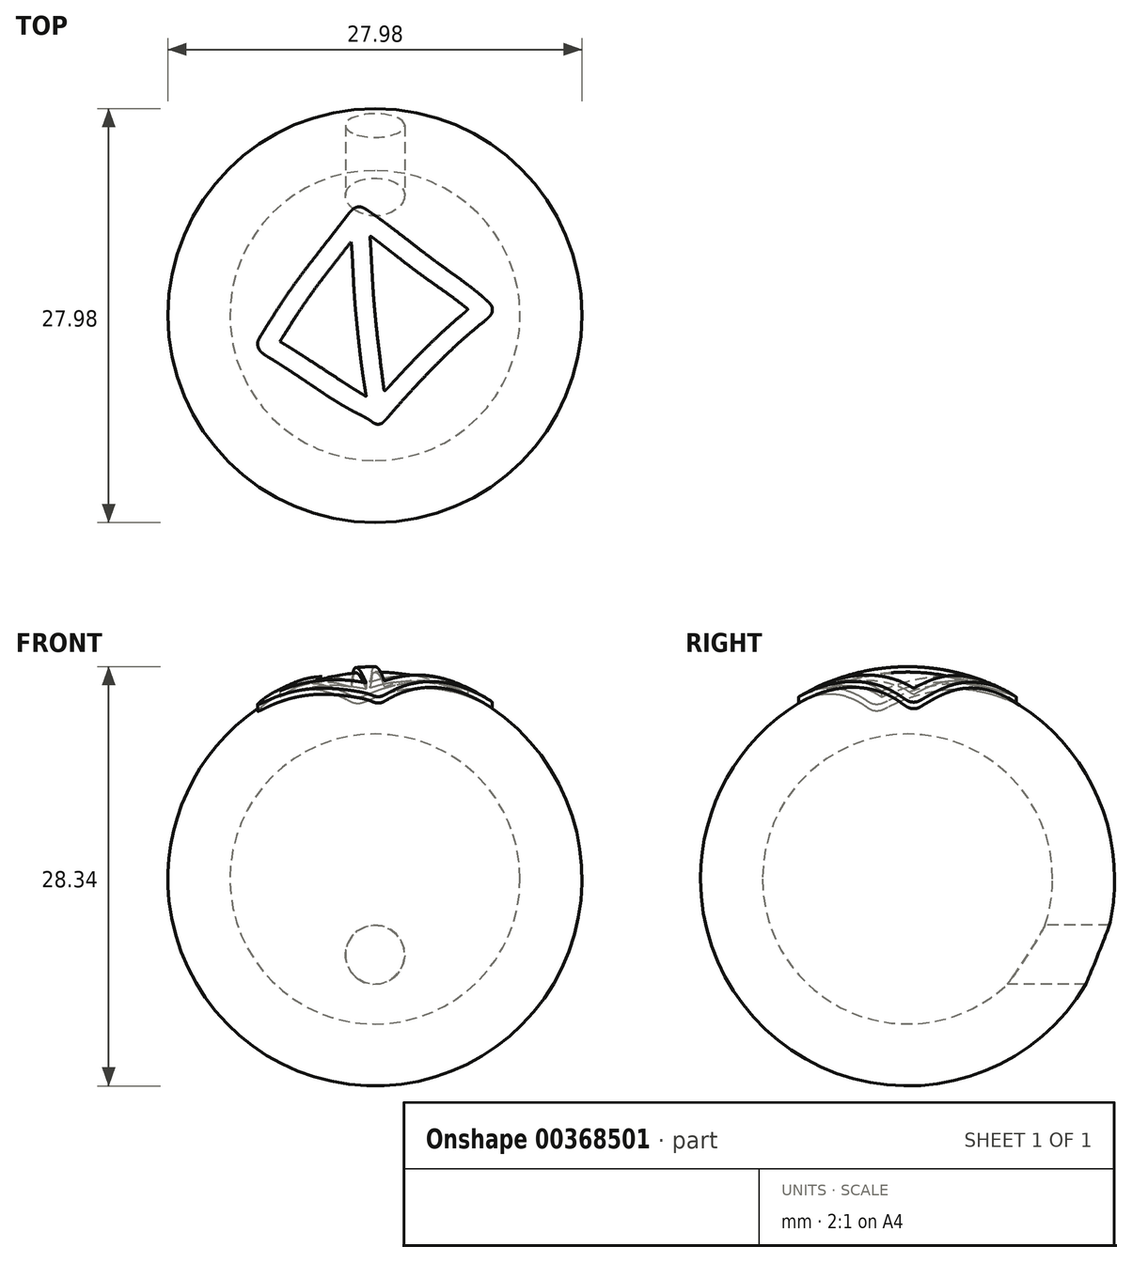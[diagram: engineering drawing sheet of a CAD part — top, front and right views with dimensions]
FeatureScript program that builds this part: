
annotation { "Feature Type Name" : "Feature", "Feature Type Description" : "" }
export const myFeature = defineFeature(function(context is Context, id is Id, definition is map)
    precondition{}
    {
        {
            var Q0;
            Q0=qCreatedBy(makeId("Top.planeOp"),FACE);
            var sketch = newSketch(context, id + "F0", { "sketchPlane" : qUnion([Q0])});
            skLineSegment(sketch, "E0", {"start": v(0, -10) * mm, "end": v(0, 10) * mm});
            skArc(sketch, "E1", {"start": v(0, 10) * mm, "mid": v(-10, 0) * mm, "end": v(0, -10) * mm});
            skSolve(sketch);
        }
        {
            var Q0;
            {var subQ0=sQuery(id+"F0.wireOp",EDGE,"E1");Q0=makeQuery(id+"F0.imprint","IMPRINT",FACE,{"disambiguationData":[TD([[makeQuery(id+"F0.imprint","IMPRINT",EDGE,{"derivedFrom":subQ0}),1.0]])]});}
            var Q1;
            Q1=sQuery(id+"F0.wireOp",EDGE,"E0");
            revolve(context, id + "F1", {"entities" : qUnion([Q0]), "axis" : qUnion([Q1]), "revolveType" : RevolveType.FULL});
        }
        {
            var Q0;
            Q0=makeQuery(id+"F1.opRevolve","SWEPT_BODY",BODY,{"disambiguationData":[OSD([sQuery(id+"F0.wireOp",EDGE,"E0"),sQuery(id+"F0.wireOp",EDGE,"E1")])]});
            var Q1;
            Q1=sQuery(id+"F0.wireOp",VERTEX,"NPe4G0ez-t7S9-9isL-QO5v-uuJu600mHcIT.center");
            var Q2;
            Q2=sQuery(id+"F0.wireOp",VERTEX,"E1.center");
            transform(context, id + "F2", {"entities" : qUnion([Q0]), "transformType" : TransformType.SCALE_UNIFORMLY, "scale" : 33.3, "scalePoint" : qUnion([Q2]), "makeCopy" : false});
        }
        {
            var Q0;
            Q0=qCreatedBy(makeId("Top.planeOp"),FACE);
            var sketch = newSketch(context, id + "F3", { "sketchPlane" : qUnion([Q0])});
            skArc(sketch, "E2", {"start": v(-33, 172.81) * mm, "mid": v(-34.37, 171.98) * mm, "end": v(-35.66, 171) * mm});
            skArc(sketch, "E3", {"start": v(-35.66, 171) * mm, "mid": v(-37.15, 169.67) * mm, "end": v(-38.56, 168.26) * mm});
            skArc(sketch, "E4", {"start": v(-38.56, 168.26) * mm, "mid": v(-40.37, 166.25) * mm, "end": v(-42.1, 164.18) * mm});
            skArc(sketch, "E5", {"start": v(-42.1, 164.18) * mm, "mid": v(-44.55, 161.1) * mm, "end": v(-46.95, 157.98) * mm});
            skArc(sketch, "E6", {"start": v(-46.95, 157.98) * mm, "mid": v(-49.6, 154.52) * mm, "end": v(-52.25, 151.08) * mm});
            skArc(sketch, "E7", {"start": v(-52.25, 151.08) * mm, "mid": v(-56.88, 145.1) * mm, "end": v(-61.52, 139.12) * mm});
            skArc(sketch, "E8", {"start": v(-61.52, 139.12) * mm, "mid": v(-66.9, 132.2) * mm, "end": v(-72.28, 125.28) * mm});
            skArc(sketch, "E9", {"start": v(-72.28, 125.28) * mm, "mid": v(-77.76, 118.26) * mm, "end": v(-83.25, 111.24) * mm});
            skArc(sketch, "E10", {"start": v(-83.25, 111.24) * mm, "mid": v(-97.95, 92.31) * mm, "end": v(-112.54, 73.3) * mm});
            skArc(sketch, "E11", {"start": v(-112.54, 73.3) * mm, "mid": v(-122.82, 59.57) * mm, "end": v(-132.87, 45.67) * mm});
            skArc(sketch, "E12", {"start": v(-132.87, 45.67) * mm, "mid": v(-142, 32.54) * mm, "end": v(-150.9, 19.25) * mm});
            skArc(sketch, "E13", {"start": v(-150.9, 19.25) * mm, "mid": v(-161.66, 2.63) * mm, "end": v(-172.26, -14.1) * mm});
            skArc(sketch, "E14", {"start": v(-172.26, -14.1) * mm, "mid": v(-177.97, -23.22) * mm, "end": v(-183.64, -32.36) * mm});
            skArc(sketch, "E15", {"start": v(-183.64, -32.36) * mm, "mid": v(-185.48, -35.48) * mm, "end": v(-187.18, -38.67) * mm});
            skArc(sketch, "E16", {"start": v(-187.18, -38.67) * mm, "mid": v(-188, -40.65) * mm, "end": v(-188.56, -42.72) * mm});
            skArc(sketch, "E17", {"start": v(-188.56, -42.72) * mm, "mid": v(-188.82, -44.8) * mm, "end": v(-188.77, -46.88) * mm});
            skArc(sketch, "E18", {"start": v(-188.77, -46.88) * mm, "mid": v(-188.23, -49.88) * mm, "end": v(-187.2, -52.73) * mm});
            skArc(sketch, "E19", {"start": v(-187.2, -52.73) * mm, "mid": v(-185.68, -55.44) * mm, "end": v(-183.75, -57.87) * mm});
            skArc(sketch, "E20", {"start": v(-183.75, -57.87) * mm, "mid": v(-180.92, -60.6) * mm, "end": v(-177.8, -63) * mm});
            skArc(sketch, "E21", {"start": v(-177.8, -63) * mm, "mid": v(-173.08, -66.1) * mm, "end": v(-168.25, -69) * mm});
            skArc(sketch, "E22", {"start": v(-168.25, -69) * mm, "mid": v(-164.73, -71.07) * mm, "end": v(-161.26, -73.21) * mm});
            skArc(sketch, "E23", {"start": v(-161.26, -73.21) * mm, "mid": v(-155.32, -76.99) * mm, "end": v(-149.4, -80.79) * mm});
            skArc(sketch, "E24", {"start": v(-149.4, -80.79) * mm, "mid": v(-142.56, -85.22) * mm, "end": v(-135.75, -89.69) * mm});
            skArc(sketch, "E25", {"start": v(-135.75, -89.69) * mm, "mid": v(-128.86, -94.25) * mm, "end": v(-122, -98.84) * mm});
            skArc(sketch, "E26", {"start": v(-122, -98.84) * mm, "mid": v(-115.2, -103.41) * mm, "end": v(-108.4, -107.98) * mm});
            skArc(sketch, "E27", {"start": v(-108.4, -107.98) * mm, "mid": v(-101.82, -112.4) * mm, "end": v(-95.25, -116.8) * mm});
            skArc(sketch, "E28", {"start": v(-95.25, -116.8) * mm, "mid": v(-89.63, -120.57) * mm, "end": v(-84.02, -124.33) * mm});
            skArc(sketch, "E29", {"start": v(-84.02, -124.33) * mm, "mid": v(-81, -126.34) * mm, "end": v(-78, -128.35) * mm});
            skArc(sketch, "E30", {"start": v(-78, -128.35) * mm, "mid": v(-71.4, -132.67) * mm, "end": v(-64.72, -136.88) * mm});
            skArc(sketch, "E31", {"start": v(-64.72, -136.88) * mm, "mid": v(-57.8, -141.12) * mm, "end": v(-50.8, -145.26) * mm});
            skArc(sketch, "E32", {"start": v(-50.8, -145.26) * mm, "mid": v(-44.03, -149.14) * mm, "end": v(-37.21, -152.92) * mm});
            skArc(sketch, "E33", {"start": v(-37.21, -152.92) * mm, "mid": v(-31.14, -156.15) * mm, "end": v(-25, -159.25) * mm});
            skArc(sketch, "E34", {"start": v(-25, -159.25) * mm, "mid": v(-22.06, -160.7) * mm, "end": v(-19.16, -162.22) * mm});
            skArc(sketch, "E35", {"start": v(-19.16, -162.22) * mm, "mid": v(-16.38, -163.71) * mm, "end": v(-13.63, -165.25) * mm});
            skArc(sketch, "E36", {"start": v(-13.63, -165.25) * mm, "mid": v(-11.31, -166.6) * mm, "end": v(-9.01, -168) * mm});
            skArc(sketch, "E37", {"start": v(-9.01, -168) * mm, "mid": v(-7.81, -168.8) * mm, "end": v(-6.69, -169.7) * mm});
            skArc(sketch, "E38", {"start": v(-6.69, -169.7) * mm, "mid": v(-4.48, -171.46) * mm, "end": v(-2.12, -173) * mm});
            skArc(sketch, "E39", {"start": v(-2.12, -173) * mm, "mid": v(0.04, -174.03) * mm, "end": v(2.34, -174.72) * mm});
            skArc(sketch, "E40", {"start": v(2.34, -174.72) * mm, "mid": v(4.5, -174.99) * mm, "end": v(6.69, -174.86) * mm});
            skArc(sketch, "E41", {"start": v(6.69, -174.86) * mm, "mid": v(8.87, -174.35) * mm, "end": v(10.94, -173.5) * mm});
            skArc(sketch, "E42", {"start": v(10.94, -173.5) * mm, "mid": v(11.75, -173) * mm, "end": v(12.5, -172.4) * mm});
            skArc(sketch, "E43", {"start": v(12.5, -172.4) * mm, "mid": v(13.95, -171) * mm, "end": v(15.38, -169.59) * mm});
            skArc(sketch, "E44", {"start": v(15.38, -169.59) * mm, "mid": v(17.06, -167.86) * mm, "end": v(18.7, -166.1) * mm});
            skArc(sketch, "E45", {"start": v(18.7, -166.1) * mm, "mid": v(20.42, -164.19) * mm, "end": v(22.1, -162.24) * mm});
            skArc(sketch, "E46", {"start": v(22.1, -162.24) * mm, "mid": v(32.46, -150.21) * mm, "end": v(42.96, -138.3) * mm});
            skArc(sketch, "E47", {"start": v(42.96, -138.3) * mm, "mid": v(54.31, -125.7) * mm, "end": v(65.78, -113.23) * mm});
            skArc(sketch, "E48", {"start": v(65.78, -113.23) * mm, "mid": v(77.16, -101.09) * mm, "end": v(88.65, -89.06) * mm});
            skArc(sketch, "E49", {"start": v(88.65, -89.06) * mm, "mid": v(99.07, -78.41) * mm, "end": v(109.64, -67.9) * mm});
            skArc(sketch, "E50", {"start": v(109.64, -67.9) * mm, "mid": v(117.81, -59.96) * mm, "end": v(126.06, -52.09) * mm});
            skArc(sketch, "E51", {"start": v(126.06, -52.09) * mm, "mid": v(133.02, -45.6) * mm, "end": v(140.08, -39.23) * mm});
            skArc(sketch, "E52", {"start": v(140.08, -39.23) * mm, "mid": v(147.61, -32.64) * mm, "end": v(155.23, -26.15) * mm});
            skArc(sketch, "E53", {"start": v(155.23, -26.15) * mm, "mid": v(165.3, -17.77) * mm, "end": v(175.42, -9.46) * mm});
            skArc(sketch, "E54", {"start": v(175.42, -9.46) * mm, "mid": v(179.05, -6.39) * mm, "end": v(182.58, -3.2) * mm});
            skArc(sketch, "E55", {"start": v(182.58, -3.2) * mm, "mid": v(184.71, -0.94) * mm, "end": v(186.58, 1.54) * mm});
            skArc(sketch, "E56", {"start": v(186.58, 1.54) * mm, "mid": v(187.71, 3.63) * mm, "end": v(188.46, 5.89) * mm});
            skArc(sketch, "E57", {"start": v(188.46, 5.89) * mm, "mid": v(188.81, 8.25) * mm, "end": v(188.75, 10.64) * mm});
            skArc(sketch, "E58", {"start": v(188.75, 10.64) * mm, "mid": v(188.42, 12.49) * mm, "end": v(187.86, 14.28) * mm});
            skArc(sketch, "E59", {"start": v(187.86, 14.28) * mm, "mid": v(187.09, 15.92) * mm, "end": v(186.1, 17.44) * mm});
            skArc(sketch, "E60", {"start": v(186.1, 17.44) * mm, "mid": v(184.48, 19.41) * mm, "end": v(182.72, 21.24) * mm});
            skArc(sketch, "E61", {"start": v(182.72, 21.24) * mm, "mid": v(179.3, 24.49) * mm, "end": v(175.84, 27.68) * mm});
            skArc(sketch, "E62", {"start": v(175.84, 27.68) * mm, "mid": v(171.1, 31.88) * mm, "end": v(166.27, 35.95) * mm});
            skArc(sketch, "E63", {"start": v(166.27, 35.95) * mm, "mid": v(160.23, 40.83) * mm, "end": v(154.12, 45.63) * mm});
            skArc(sketch, "E64", {"start": v(154.12, 45.63) * mm, "mid": v(146.93, 51.13) * mm, "end": v(139.67, 56.53) * mm});
            skArc(sketch, "E65", {"start": v(139.67, 56.53) * mm, "mid": v(131.36, 62.6) * mm, "end": v(123, 68.58) * mm});
            skArc(sketch, "E66", {"start": v(123, 68.58) * mm, "mid": v(114.4, 74.72) * mm, "end": v(105.83, 80.91) * mm});
            skArc(sketch, "E67", {"start": v(105.83, 80.91) * mm, "mid": v(98.5, 86.27) * mm, "end": v(91.21, 91.69) * mm});
            skArc(sketch, "E68", {"start": v(91.21, 91.69) * mm, "mid": v(83.18, 97.75) * mm, "end": v(75.19, 103.87) * mm});
            skArc(sketch, "E69", {"start": v(75.19, 103.87) * mm, "mid": v(64.09, 112.45) * mm, "end": v(53, 121.05) * mm});
            skArc(sketch, "E70", {"start": v(53, 121.05) * mm, "mid": v(42.99, 128.83) * mm, "end": v(32.94, 136.58) * mm});
            skArc(sketch, "E71", {"start": v(32.94, 136.58) * mm, "mid": v(25.36, 142.38) * mm, "end": v(17.73, 148.12) * mm});
            skArc(sketch, "E72", {"start": v(17.73, 148.12) * mm, "mid": v(11.29, 152.88) * mm, "end": v(4.8, 157.6) * mm});
            skArc(sketch, "E73", {"start": v(4.8, 157.6) * mm, "mid": v(-1.5, 162.08) * mm, "end": v(-7.86, 166.51) * mm});
            skArc(sketch, "E74", {"start": v(-7.86, 166.51) * mm, "mid": v(-12.3, 169.46) * mm, "end": v(-16.82, 172.26) * mm});
            skArc(sketch, "E75", {"start": v(-16.82, 172.26) * mm, "mid": v(-19.64, 173.67) * mm, "end": v(-22.64, 174.66) * mm});
            skArc(sketch, "E76", {"start": v(-22.64, 174.66) * mm, "mid": v(-25.1, 175) * mm, "end": v(-27.56, 174.77) * mm});
            skArc(sketch, "E77", {"start": v(-27.56, 174.77) * mm, "mid": v(-30.35, 173.98) * mm, "end": v(-33, 172.81) * mm});
            skArc(sketch, "E78", {"start": v(2.5, 120.65) * mm, "mid": v(4.7, 119) * mm, "end": v(6.88, 117.32) * mm});
            skArc(sketch, "E79", {"start": v(6.88, 117.32) * mm, "mid": v(10.53, 114.5) * mm, "end": v(14.18, 111.67) * mm});
            skArc(sketch, "E80", {"start": v(14.18, 111.67) * mm, "mid": v(18.38, 108.4) * mm, "end": v(22.57, 105.14) * mm});
            skArc(sketch, "E81", {"start": v(22.57, 105.14) * mm, "mid": v(26.8, 101.84) * mm, "end": v(31, 98.53) * mm});
            skArc(sketch, "E82", {"start": v(31, 98.53) * mm, "mid": v(40.47, 91.14) * mm, "end": v(49.96, 83.78) * mm});
            skArc(sketch, "E83", {"start": v(49.96, 83.78) * mm, "mid": v(57.43, 78.07) * mm, "end": v(64.95, 72.41) * mm});
            skArc(sketch, "E84", {"start": v(64.95, 72.41) * mm, "mid": v(72.33, 66.96) * mm, "end": v(79.75, 61.57) * mm});
            skArc(sketch, "E85", {"start": v(79.75, 61.57) * mm, "mid": v(88.87, 55.05) * mm, "end": v(98, 48.58) * mm});
            skArc(sketch, "E86", {"start": v(98, 48.58) * mm, "mid": v(108.94, 40.81) * mm, "end": v(119.82, 32.97) * mm});
            skArc(sketch, "E87", {"start": v(119.82, 32.97) * mm, "mid": v(127.9, 27) * mm, "end": v(135.87, 20.91) * mm});
            skArc(sketch, "E88", {"start": v(135.87, 20.91) * mm, "mid": v(142.08, 16.05) * mm, "end": v(148.26, 11.14) * mm});
            skArc(sketch, "E89", {"start": v(148.26, 11.14) * mm, "mid": v(148.87, 10.2) * mm, "end": v(148.8, 9.07) * mm});
            skArc(sketch, "E90", {"start": v(148.8, 9.07) * mm, "mid": v(148.66, 8.82) * mm, "end": v(148.47, 8.6) * mm});
            skArc(sketch, "E91", {"start": v(148.47, 8.6) * mm, "mid": v(147.14, 7.42) * mm, "end": v(145.8, 6.25) * mm});
            skArc(sketch, "E92", {"start": v(145.8, 6.25) * mm, "mid": v(144.24, 4.89) * mm, "end": v(142.67, 3.54) * mm});
            skArc(sketch, "E93", {"start": v(142.67, 3.54) * mm, "mid": v(140.84, 2) * mm, "end": v(139, 0.47) * mm});
            skArc(sketch, "E94", {"start": v(139, 0.47) * mm, "mid": v(126.28, -10.36) * mm, "end": v(113.83, -21.52) * mm});
            skArc(sketch, "E95", {"start": v(113.83, -21.52) * mm, "mid": v(99.63, -34.82) * mm, "end": v(85.65, -48.36) * mm});
            skArc(sketch, "E96", {"start": v(85.65, -48.36) * mm, "mid": v(70.67, -63.33) * mm, "end": v(55.94, -78.53) * mm});
            skArc(sketch, "E97", {"start": v(55.94, -78.53) * mm, "mid": v(40.89, -94.52) * mm, "end": v(26.07, -110.7) * mm});
            skArc(sketch, "E98", {"start": v(26.07, -110.7) * mm, "mid": v(24.28, -112.68) * mm, "end": v(22.47, -114.64) * mm});
            skArc(sketch, "E99", {"start": v(22.47, -114.64) * mm, "mid": v(20.9, -116.3) * mm, "end": v(19.32, -117.95) * mm});
            skArc(sketch, "E100", {"start": v(19.32, -117.95) * mm, "mid": v(17.95, -119.36) * mm, "end": v(16.56, -120.76) * mm});
            skArc(sketch, "E101", {"start": v(16.56, -120.76) * mm, "mid": v(16.35, -120.9) * mm, "end": v(16.1, -120.96) * mm});
            skArc(sketch, "E102", {"start": v(16.1, -120.96) * mm, "mid": v(14.93, -120.52) * mm, "end": v(14.34, -119.42) * mm});
            skArc(sketch, "E103", {"start": v(14.34, -119.42) * mm, "mid": v(11.4, -96.18) * mm, "end": v(8.47, -72.95) * mm});
            skArc(sketch, "E104", {"start": v(8.47, -72.95) * mm, "mid": v(5.63, -49.46) * mm, "end": v(2.99, -25.95) * mm});
            skArc(sketch, "E105", {"start": v(2.99, -25.95) * mm, "mid": v(0.67, -3.46) * mm, "end": v(-1.44, 19.04) * mm});
            skArc(sketch, "E106", {"start": v(-1.44, 19.04) * mm, "mid": v(-1.82, 23.65) * mm, "end": v(-2.17, 28.26) * mm});
            skArc(sketch, "E107", {"start": v(-2.17, 28.26) * mm, "mid": v(-2.65, 35.41) * mm, "end": v(-3.12, 42.56) * mm});
            skArc(sketch, "E108", {"start": v(-3.12, 42.56) * mm, "mid": v(-3.62, 50.64) * mm, "end": v(-4.1, 58.71) * mm});
            skArc(sketch, "E109", {"start": v(-4.1, 58.71) * mm, "mid": v(-4.55, 66.63) * mm, "end": v(-4.98, 74.54) * mm});
            skArc(sketch, "E110", {"start": v(-4.98, 74.54) * mm, "mid": v(-5.38, 82.1) * mm, "end": v(-5.8, 89.67) * mm});
            skArc(sketch, "E111", {"start": v(-5.8, 89.67) * mm, "mid": v(-6.18, 96.69) * mm, "end": v(-6.58, 103.7) * mm});
            skArc(sketch, "E112", {"start": v(-6.58, 103.7) * mm, "mid": v(-6.92, 109.59) * mm, "end": v(-7.27, 115.47) * mm});
            skArc(sketch, "E113", {"start": v(-7.27, 115.47) * mm, "mid": v(-7.43, 117.96) * mm, "end": v(-7.62, 120.44) * mm});
            skArc(sketch, "E114", {"start": v(-7.62, 120.44) * mm, "mid": v(-7.85, 123.46) * mm, "end": v(-8.01, 126.48) * mm});
            skArc(sketch, "E115", {"start": v(-8.01, 126.48) * mm, "mid": v(-7.8, 127.05) * mm, "end": v(-7.26, 127.3) * mm});
            skArc(sketch, "E116", {"start": v(-7.26, 127.3) * mm, "mid": v(-6.45, 127.17) * mm, "end": v(-5.73, 126.8) * mm});
            skArc(sketch, "E117", {"start": v(-5.73, 126.8) * mm, "mid": v(-1.6, 123.74) * mm, "end": v(2.5, 120.65) * mm});
            skArc(sketch, "E118", {"start": v(-35.55, 75.04) * mm, "mid": v(-34.77, 59.8) * mm, "end": v(-33.94, 44.56) * mm});
            skArc(sketch, "E119", {"start": v(-33.94, 44.56) * mm, "mid": v(-33.32, 34.26) * mm, "end": v(-32.6, 23.96) * mm});
            skArc(sketch, "E120", {"start": v(-32.6, 23.96) * mm, "mid": v(-31.84, 14.28) * mm, "end": v(-30.97, 4.61) * mm});
            skArc(sketch, "E121", {"start": v(-30.97, 4.61) * mm, "mid": v(-29.73, -8.18) * mm, "end": v(-28.43, -20.96) * mm});
            skArc(sketch, "E122", {"start": v(-28.43, -20.96) * mm, "mid": v(-26.87, -35.75) * mm, "end": v(-25.25, -50.53) * mm});
            skArc(sketch, "E123", {"start": v(-25.25, -50.53) * mm, "mid": v(-23.89, -62.47) * mm, "end": v(-22.44, -74.39) * mm});
            skArc(sketch, "E124", {"start": v(-22.44, -74.39) * mm, "mid": v(-21.14, -84.39) * mm, "end": v(-19.77, -94.38) * mm});
            skArc(sketch, "E125", {"start": v(-19.77, -94.38) * mm, "mid": v(-18.47, -103.17) * mm, "end": v(-17.06, -111.95) * mm});
            skArc(sketch, "E126", {"start": v(-17.06, -111.95) * mm, "mid": v(-16.5, -115.31) * mm, "end": v(-15.96, -118.68) * mm});
            skArc(sketch, "E127", {"start": v(-15.96, -118.68) * mm, "mid": v(-15.5, -121.53) * mm, "end": v(-15.07, -124.38) * mm});
            skArc(sketch, "E128", {"start": v(-15.07, -124.38) * mm, "mid": v(-14.7, -126.92) * mm, "end": v(-14.32, -129.45) * mm});
            skArc(sketch, "E129", {"start": v(-14.32, -129.45) * mm, "mid": v(-14.33, -129.58) * mm, "end": v(-14.4, -129.7) * mm});
            skArc(sketch, "E130", {"start": v(-14.4, -129.7) * mm, "mid": v(-14.77, -129.88) * mm, "end": v(-15.17, -129.79) * mm});
            skArc(sketch, "E131", {"start": v(-15.17, -129.79) * mm, "mid": v(-21.77, -125.75) * mm, "end": v(-28.36, -121.71) * mm});
            skArc(sketch, "E132", {"start": v(-28.36, -121.71) * mm, "mid": v(-35.1, -117.53) * mm, "end": v(-41.81, -113.3) * mm});
            skArc(sketch, "E133", {"start": v(-41.81, -113.3) * mm, "mid": v(-48.42, -109.06) * mm, "end": v(-55, -104.77) * mm});
            skArc(sketch, "E134", {"start": v(-55, -104.77) * mm, "mid": v(-69.13, -95.47) * mm, "end": v(-83.29, -86.18) * mm});
            skArc(sketch, "E135", {"start": v(-83.29, -86.18) * mm, "mid": v(-95.7, -78.09) * mm, "end": v(-108.12, -70.02) * mm});
            skArc(sketch, "E136", {"start": v(-108.12, -70.02) * mm, "mid": v(-118.2, -63.5) * mm, "end": v(-128.3, -57.02) * mm});
            skArc(sketch, "E137", {"start": v(-128.3, -57.02) * mm, "mid": v(-134.23, -53.26) * mm, "end": v(-140.2, -49.57) * mm});
            skLineSegment(sketch, "E138", {"start": v(-140.2, -49.57) * mm, "end": v(-152.92, -41.82) * mm});
            skLineSegment(sketch, "E139", {"start": v(-152.92, -41.82) * mm, "end": v(-147.8, -33.64) * mm});
            skArc(sketch, "E140", {"start": v(-147.8, -33.64) * mm, "mid": v(-136.62, -15.94) * mm, "end": v(-125.26, 1.64) * mm});
            skArc(sketch, "E141", {"start": v(-125.26, 1.64) * mm, "mid": v(-115.72, 15.96) * mm, "end": v(-105.93, 30.11) * mm});
            skArc(sketch, "E142", {"start": v(-105.93, 30.11) * mm, "mid": v(-95.68, 44.37) * mm, "end": v(-85.19, 58.46) * mm});
            skArc(sketch, "E143", {"start": v(-85.19, 58.46) * mm, "mid": v(-71.73, 76.03) * mm, "end": v(-58.12, 93.49) * mm});
            skLineSegment(sketch, "E144", {"start": v(-58.12, 93.49) * mm, "end": v(-38.5, 118.44) * mm});
            skLineSegment(sketch, "E145", {"start": v(-38.5, 118.44) * mm, "end": v(-37.83, 112.99) * mm});
            skArc(sketch, "E146", {"start": v(-37.83, 112.99) * mm, "mid": v(-37.63, 111.2) * mm, "end": v(-37.5, 109.4) * mm});
            skArc(sketch, "E147", {"start": v(-37.5, 109.4) * mm, "mid": v(-37.18, 104.5) * mm, "end": v(-36.88, 99.6) * mm});
            skArc(sketch, "E148", {"start": v(-36.88, 99.6) * mm, "mid": v(-36.54, 93.74) * mm, "end": v(-36.22, 87.89) * mm});
            skArc(sketch, "E149", {"start": v(-36.22, 87.89) * mm, "mid": v(-35.88, 81.47) * mm, "end": v(-35.55, 75.04) * mm});
            skSolve(sketch);
        }
        {
            var Q0;
            Q0=qSketchRegion(id+"F3",true);
            var Q1;
            Q1=sQuery(id+"F3.wireOp",EDGE,"c928f899-12af-4b01-b412-b3b7da3d830f");
            var Q2;
            Q2=sQuery(id+"F3.wireOp",EDGE,"b69f99c7-a6d0-4d1b-8752-9e82ab4c99ec");
            extrude(context, id + "F4", {"entities" : qUnion([Q0]), "operationType" : NewBodyOperationType.ADD, "surfaceEntities" : qUnion([Q1, Q2]), "depth" : 350 * mm});
        }
        {
            var Q0;
            Q0=makeQuery(id+"F4.opExtrude","SWEPT_BODY",BODY,{"disambiguationData":[OSD([sQuery(id+"F3.wireOp",EDGE,"15c6da4e-992d-4824-9d20-70d2d6be9970"),sQuery(id+"F3.wireOp",EDGE,"268c69ec-46be-456f-85eb-69decc32fe39"),sQuery(id+"F3.wireOp",EDGE,"1d386307-6059-4203-bca6-0c1cec3c82e1"),sQuery(id+"F3.wireOp",EDGE,"7d7c66d2-f869-427f-806b-ad436cacd60e"),sQuery(id+"F3.wireOp",EDGE,"1db91850-860e-493f-a3af-7a0f3f1512ae"),sQuery(id+"F3.wireOp",EDGE,"2c65f23b-9f03-4f6f-ab37-de452af29e3c"),sQuery(id+"F3.wireOp",EDGE,"ba006cbc-bbd7-44d9-84cc-9cde0967c280"),sQuery(id+"F3.wireOp",EDGE,"ae950208-c781-4a25-8fcf-ffe59b9085ff"),sQuery(id+"F3.wireOp",EDGE,"3cce0944-c62d-4831-9b9d-d1a418d328b4"),sQuery(id+"F3.wireOp",EDGE,"9edc5e7d-16c0-40c4-98ad-6b91d5df0e78"),sQuery(id+"F3.wireOp",EDGE,"aa452f44-44a2-4c64-bff5-a2a639df00db"),sQuery(id+"F3.wireOp",EDGE,"16259f99-ce20-4b7b-81e1-fa0909c03eb4"),sQuery(id+"F3.wireOp",EDGE,"79895566-a943-429d-b257-d76af3645bdf"),sQuery(id+"F3.wireOp",EDGE,"a85490ef-f17e-45c8-b92b-28215162778a"),sQuery(id+"F3.wireOp",EDGE,"322f1036-a6fd-4992-ab69-5919540af7a6"),sQuery(id+"F3.wireOp",EDGE,"0a87ff38-4ab4-4140-b3c3-2d7501d9f3b1"),sQuery(id+"F3.wireOp",EDGE,"a6e7bdf2-ef3e-49d4-9b3c-e34f5a41e0c4"),sQuery(id+"F3.wireOp",EDGE,"3e588790-576f-47c1-9730-f5e27fa1e8f9"),sQuery(id+"F3.wireOp",EDGE,"ce3739ef-15fd-4754-ad9c-ccf511a9a8fb"),sQuery(id+"F3.wireOp",EDGE,"201134a3-66f3-4a3f-aa9b-76948966efc0"),sQuery(id+"F3.wireOp",EDGE,"65b511ea-0759-428d-8070-88e1f521d8ea"),sQuery(id+"F3.wireOp",EDGE,"c37cddb6-5cf8-4891-aff4-7191a72080b9"),sQuery(id+"F3.wireOp",EDGE,"52a43dbd-e952-43e1-be3d-d70e107260e6"),sQuery(id+"F3.wireOp",EDGE,"08c1271f-f5c3-4f26-be27-7f5e21217dff"),sQuery(id+"F3.wireOp",EDGE,"59a09f58-0503-4180-962a-e04db21f0da8"),sQuery(id+"F3.wireOp",EDGE,"e56a4626-e956-42c3-bb5d-cd9dae1ca801"),sQuery(id+"F3.wireOp",EDGE,"5ff5d55f-af90-49eb-8040-353101557de8"),sQuery(id+"F3.wireOp",EDGE,"0ed7430b-e164-4f56-8af9-4534524aa7c0"),sQuery(id+"F3.wireOp",EDGE,"b5610a6e-b6bb-43e3-9a8d-d3d7c5f0098b"),sQuery(id+"F3.wireOp",EDGE,"1d417af8-88ad-47c2-a4e2-6fec82bd6695"),sQuery(id+"F3.wireOp",EDGE,"778ae99a-956a-4ddb-8078-d9bc57f9fc8e"),sQuery(id+"F3.wireOp",EDGE,"5b19af09-f144-446e-9dfa-8766819c9efd"),sQuery(id+"F3.wireOp",EDGE,"028339f6-0475-4a57-af8d-550e32ad7466"),sQuery(id+"F3.wireOp",EDGE,"d5ae35b6-d210-433a-92c8-e92622696872"),sQuery(id+"F3.wireOp",EDGE,"16a2e606-2caa-4876-9ffa-8f08c4ff3a37"),sQuery(id+"F3.wireOp",EDGE,"5b90b144-be56-4de7-a9dd-c1e0336acbe3"),sQuery(id+"F3.wireOp",EDGE,"5912d126-c5fc-41e4-bfb8-b4fefc52ca72"),sQuery(id+"F3.wireOp",EDGE,"2e96ce95-bd3e-4f27-a7f8-b62cf5efe954"),sQuery(id+"F3.wireOp",EDGE,"ecb4e259-1207-4dd0-bc3c-87c6506cc3a5"),sQuery(id+"F3.wireOp",EDGE,"105fb72e-4d79-4204-af2f-b3b26f5eb8d1"),sQuery(id+"F3.wireOp",EDGE,"fa59b598-df54-48c6-bb8f-c5f7618c69d0"),sQuery(id+"F3.wireOp",EDGE,"a6beef0d-f124-47ac-b957-e6cd3057a354"),sQuery(id+"F3.wireOp",EDGE,"7c3eaf53-dcb7-43b1-ad18-80ff953eb59e"),sQuery(id+"F3.wireOp",EDGE,"281fe206-104f-408f-94b6-be79f12604c9")])]});
            var Q1;
            Q1=makeQuery(id+"F4.opExtrude","SWEPT_BODY",BODY,{"disambiguationData":[OSD([sQuery(id+"F3.wireOp",EDGE,"58f6206a-5554-41d4-8cf7-6e0b4724a469"),sQuery(id+"F3.wireOp",EDGE,"85dabe77-b6aa-43d5-a519-64383616f71e"),sQuery(id+"F3.wireOp",EDGE,"4b679fe6-9e11-497d-b8fd-14ca14e49ddd"),sQuery(id+"F3.wireOp",EDGE,"51de25f6-d59e-4805-a327-1fd7e38869c8"),sQuery(id+"F3.wireOp",EDGE,"d47977fb-70d3-4df8-bc35-66fcc0e556e0"),sQuery(id+"F3.wireOp",EDGE,"235006b0-8f14-4ca2-82f0-f96b6b8c4766"),sQuery(id+"F3.wireOp",EDGE,"0fc7acd6-1c1d-47a8-ba12-62eb658d35ca"),sQuery(id+"F3.wireOp",EDGE,"883fa5e3-ca4c-4ce6-a249-4debf538fe24"),sQuery(id+"F3.wireOp",EDGE,"1da09ed1-22d9-43a1-a655-8acff5d61309"),sQuery(id+"F3.wireOp",EDGE,"32654a82-a09a-444f-bf73-45f818f0f235"),sQuery(id+"F3.wireOp",EDGE,"a398fd80-a0a9-4724-ba0e-1a7a000baa92"),sQuery(id+"F3.wireOp",EDGE,"f39f97c8-53f5-4046-9905-b28daecd4f10"),sQuery(id+"F3.wireOp",EDGE,"2484d883-0ec2-4c7d-9023-165ebbef226c"),sQuery(id+"F3.wireOp",EDGE,"f026d96f-3d32-4113-a1c9-3545f5cdbe4a"),sQuery(id+"F3.wireOp",EDGE,"974fee18-719e-4620-aace-d3676da2011b"),sQuery(id+"F3.wireOp",EDGE,"0c5766d2-a026-45af-bffd-0d1f783d5157"),sQuery(id+"F3.wireOp",EDGE,"5da13fee-9c04-45d8-805f-c7a03dde2383"),sQuery(id+"F3.wireOp",EDGE,"dbea32a3-85bd-4957-aef2-b6fe64a02f6b"),sQuery(id+"F3.wireOp",EDGE,"fba134ea-bf40-4191-ad8f-cc6b2b040a97"),sQuery(id+"F3.wireOp",EDGE,"0c19e200-7cd5-4fcb-83ed-261bd7936bc7"),sQuery(id+"F3.wireOp",EDGE,"246b843b-ea86-44e5-9cb9-335e6677b61d"),sQuery(id+"F3.wireOp",EDGE,"c1b3c9bc-1eb4-4c9b-99c8-0cebed89395a"),sQuery(id+"F3.wireOp",EDGE,"f93eebc3-1447-4029-8362-91325193ac2b"),sQuery(id+"F3.wireOp",EDGE,"bf86b12d-53a9-4c19-abaa-b1e658933ceb"),sQuery(id+"F3.wireOp",EDGE,"89646a71-1a60-4e14-b80a-74fb601d0855"),sQuery(id+"F3.wireOp",EDGE,"7b03dcde-0a52-4f3c-80e9-110d1d805e93"),sQuery(id+"F3.wireOp",EDGE,"83e8d1f3-8820-485b-8b6d-3ecd79124883"),sQuery(id+"F3.wireOp",EDGE,"ec7b56eb-ca95-44fd-a774-e9b7f9d3f50d"),sQuery(id+"F3.wireOp",EDGE,"31861aa6-cfd1-43ce-a7c5-bacfb7e2a30f"),sQuery(id+"F3.wireOp",EDGE,"fa3de647-1dd9-4141-982b-74ae8d07851d"),sQuery(id+"F3.wireOp",EDGE,"75d7c1c5-761c-4178-bfd4-4f469045899b"),sQuery(id+"F3.wireOp",EDGE,"4b3d7518-bd5d-4ecc-b2c5-d8dd665de4f4"),sQuery(id+"F3.wireOp",EDGE,"3be2682d-01bd-4f31-9cde-9df16a01e4a9"),sQuery(id+"F3.wireOp",EDGE,"72d3c7a9-2794-46eb-9b0d-6c526cc1b9a3"),sQuery(id+"F3.wireOp",EDGE,"0137e336-6b26-4f8d-b9ad-47ce1aa9eb31"),sQuery(id+"F3.wireOp",EDGE,"96000e4a-2d86-4b9f-af7d-a1c875cc048c"),sQuery(id+"F3.wireOp",EDGE,"139c5a79-9c0f-4e15-b57f-4c09662495a3"),sQuery(id+"F3.wireOp",EDGE,"8ea04d8b-b3da-46bb-9742-d8cba6b23bda"),sQuery(id+"F3.wireOp",EDGE,"b352b580-467e-481c-88ac-6217b8462947"),sQuery(id+"F3.wireOp",EDGE,"2503a493-1722-4539-8d54-7329fc0b116a"),sQuery(id+"F3.wireOp",EDGE,"a0615e06-0a48-4c65-8818-f0f693937022"),sQuery(id+"F3.wireOp",EDGE,"08389002-1ce8-438a-b5a4-698ca33590c2"),sQuery(id+"F3.wireOp",EDGE,"1756e4aa-c30a-461e-962c-81ee35d31e55"),sQuery(id+"F3.wireOp",EDGE,"5f84c249-07ea-4efb-9be3-ca494937f772"),sQuery(id+"F3.wireOp",EDGE,"cbefd041-b54f-4587-87b6-437b2290d1fc"),sQuery(id+"F3.wireOp",EDGE,"d44f58d4-f1a7-4aec-b016-8e7f1e498aeb"),sQuery(id+"F3.wireOp",EDGE,"0a5be90b-7545-44ea-9f2d-c726a5a2121c"),sQuery(id+"F3.wireOp",EDGE,"0cfaa442-d102-4580-8ef6-489f2aa1e6b3")])]});
            var Q2;
            Q2=makeQuery(id+"F4.opExtrude","SWEPT_BODY",BODY,{"disambiguationData":[OSD([sQuery(id+"F3.wireOp",EDGE,"9cc7aec6-4d94-4577-ab6c-32f5aa316238"),sQuery(id+"F3.wireOp",EDGE,"5ab2d840-4a32-405a-8c4b-a8126e3e1bc1"),sQuery(id+"F3.wireOp",EDGE,"56de48b4-9620-4637-8196-310e2641530f"),sQuery(id+"F3.wireOp",EDGE,"55327826-e64b-4830-85f2-3f22d36f43b5"),sQuery(id+"F3.wireOp",EDGE,"0245b46f-a639-4a95-8ca3-1568736ceed2"),sQuery(id+"F3.wireOp",EDGE,"9bd8a002-6ca7-4c84-8984-a620eefad103"),sQuery(id+"F3.wireOp",EDGE,"d4736c5e-da0b-46a0-ba9d-17ae07bb2b66"),sQuery(id+"F3.wireOp",EDGE,"125695b8-77e6-4e99-8f78-5f8fae1a0c71"),sQuery(id+"F3.wireOp",EDGE,"c9f25b10-a495-4684-8f25-8f255fabab6e"),sQuery(id+"F3.wireOp",EDGE,"0dbee67a-2ab6-4abb-ae16-0fe64d623848"),sQuery(id+"F3.wireOp",EDGE,"92c08d8e-ed2e-41a3-9c1a-b5ddaf8a0bf1"),sQuery(id+"F3.wireOp",EDGE,"00fabb15-0c1e-492e-85c1-17390e5b12bc"),sQuery(id+"F3.wireOp",EDGE,"065a9352-dddb-4e3f-b02a-444c867b75fe"),sQuery(id+"F3.wireOp",EDGE,"ef206bb6-e4f2-4189-9fc7-a7823c329ad6"),sQuery(id+"F3.wireOp",EDGE,"7199cbbe-c9bf-4cb9-b928-2ff8a84eb09e"),sQuery(id+"F3.wireOp",EDGE,"17bf9ed1-b881-4f74-816d-3511b6b328c7"),sQuery(id+"F3.wireOp",EDGE,"e5b615d0-4193-495d-b285-bd69ae30f000"),sQuery(id+"F3.wireOp",EDGE,"cfeaf62f-6be1-426b-9732-01e1a667be7e"),sQuery(id+"F3.wireOp",EDGE,"ac56344b-5ee6-4fa5-8e47-65b2a4ea3a01"),sQuery(id+"F3.wireOp",EDGE,"45b5fa53-15fd-43a0-91b0-943cc3286fc9")])]});
            var Q3;
            Q3=makeQuery(id+"F4.opExtrude","SWEPT_BODY",BODY,{"disambiguationData":[OSD([sQuery(id+"F3.wireOp",EDGE,"7bdfe37d-9957-4663-8239-5490fd3220d9"),sQuery(id+"F3.wireOp",EDGE,"6a91314f-c002-4565-bbf8-bb9f29165fb8"),sQuery(id+"F3.wireOp",EDGE,"b69f99c7-a6d0-4d1b-8752-9e82ab4c99ec"),sQuery(id+"F3.wireOp",EDGE,"c928f899-12af-4b01-b412-b3b7da3d830f"),sQuery(id+"F3.wireOp",EDGE,"ffa58721-cdd5-406d-be26-d96f7a050df4"),sQuery(id+"F3.wireOp",EDGE,"02fc7fb8-293b-44ff-ab78-63506d0aedb9"),sQuery(id+"F3.wireOp",EDGE,"147fb6cb-2565-4fb5-9280-6afbf9eef36b"),sQuery(id+"F3.wireOp",EDGE,"2cee3704-4124-415a-b391-31af1cf305d7"),sQuery(id+"F3.wireOp",EDGE,"32b2fb71-03c8-4978-9d95-2b5aaf044d0d"),sQuery(id+"F3.wireOp",EDGE,"e5d05796-7d6c-4350-8a4e-d55f5ade2f77"),sQuery(id+"F3.wireOp",EDGE,"77b1164c-8dd4-4680-b616-ac151a422eb2"),sQuery(id+"F3.wireOp",EDGE,"ec0798b8-0fbb-49ea-9766-39d2ee0936b0"),sQuery(id+"F3.wireOp",EDGE,"c4af6478-2a03-47a6-862f-c0c71886b8a3"),sQuery(id+"F3.wireOp",EDGE,"1912a38f-fa28-45c6-ab33-84cac2787056"),sQuery(id+"F3.wireOp",EDGE,"5d79fa95-f66d-4d2b-923b-4d54735f1fbd"),sQuery(id+"F3.wireOp",EDGE,"2db7aef4-a710-4bcf-9c1c-a8a87719953d"),sQuery(id+"F3.wireOp",EDGE,"183449de-345c-4115-9bca-43a403e62dbd"),sQuery(id+"F3.wireOp",EDGE,"e3ac8c9b-cab5-44b0-ad81-0e2b680c384a"),sQuery(id+"F3.wireOp",EDGE,"92e85db6-f458-41f6-a9a1-1e1a1a7e7809"),sQuery(id+"F3.wireOp",EDGE,"f0dbb46f-43a9-447b-9c75-8dfc9b95470d"),sQuery(id+"F3.wireOp",EDGE,"4b73f5f6-f769-4414-bdba-7d253e58fff4"),sQuery(id+"F3.wireOp",EDGE,"a88669dc-35b3-46bb-964f-c9bf6c4ab898"),sQuery(id+"F3.wireOp",EDGE,"2c559bae-f38f-4377-91e6-3c9de70acf11"),sQuery(id+"F3.wireOp",EDGE,"c1caf99b-adaa-42fe-a319-8cbcd819cf89"),sQuery(id+"F3.wireOp",EDGE,"54b04dd4-0ec4-4956-b19c-1141095738e3"),sQuery(id+"F3.wireOp",EDGE,"098f7a84-b7b8-4879-b21a-5c38879e4110"),sQuery(id+"F3.wireOp",EDGE,"b406a8e6-a226-4f3d-ac30-e4d06e4dac62"),sQuery(id+"F3.wireOp",EDGE,"36f95d1d-68ce-4231-ad71-3960c85e5915"),sQuery(id+"F3.wireOp",EDGE,"dc12cad8-2eed-454e-aa74-30099b1c9064"),sQuery(id+"F3.wireOp",EDGE,"4c78a4fd-cd81-43d6-85d6-6e4d3fbc1e98"),sQuery(id+"F3.wireOp",EDGE,"ee9e30de-787b-4e8f-b425-43a8e9289f81"),sQuery(id+"F3.wireOp",EDGE,"2518a3a4-c96b-4463-8704-0b71c65c60d2"),sQuery(id+"F3.wireOp",EDGE,"c9129a67-398c-4e37-92cb-2d54ff2e2e82"),sQuery(id+"F3.wireOp",EDGE,"d429d547-9f5b-42c6-bcca-effad2fa908f"),sQuery(id+"F3.wireOp",EDGE,"99d16e94-b2b3-43d5-9c7b-7bd463994dcb"),sQuery(id+"F3.wireOp",EDGE,"32993909-9a70-47ee-9097-89fff220f839"),sQuery(id+"F3.wireOp",EDGE,"6eabbeed-9496-4825-b168-63782a34f495"),sQuery(id+"F3.wireOp",EDGE,"f74987e3-8e60-4a5b-857f-839ae8aaf0cf"),sQuery(id+"F3.wireOp",EDGE,"1c218c86-035d-4441-93c0-9621d3297c3a"),sQuery(id+"F3.wireOp",EDGE,"0133f513-4b11-4cc4-b075-4625e9591e41"),sQuery(id+"F3.wireOp",EDGE,"fe921ad4-a8f5-4772-9aeb-350aca2e8948"),sQuery(id+"F3.wireOp",EDGE,"bfde0a4f-3cec-4f8e-8a23-dd1441b34c2b"),sQuery(id+"F3.wireOp",EDGE,"b41521ff-c5df-4b64-83ed-5e7635cf4438"),sQuery(id+"F3.wireOp",EDGE,"ed692599-6bbb-4379-8e89-ea326a0a0f87"),sQuery(id+"F3.wireOp",EDGE,"a98451c0-d76c-436e-99f9-a3fe9c8430a4"),sQuery(id+"F3.wireOp",EDGE,"561965b2-3050-4f49-9305-d98a2b852bbe"),sQuery(id+"F3.wireOp",EDGE,"e13dfa59-48e6-4b4e-94b9-1fc5254b0f2e"),sQuery(id+"F3.wireOp",EDGE,"0354e106-253a-4bfa-b5b7-b09cd0f2f6c0"),sQuery(id+"F3.wireOp",EDGE,"8df1dcc8-d00a-4777-85fd-8af8e9830bd1"),sQuery(id+"F3.wireOp",EDGE,"26ce3762-0d1a-4b81-9a23-debcfc24da1c"),sQuery(id+"F3.wireOp",EDGE,"3e900f8f-3ffb-4e32-b536-61fea2f3e30a"),sQuery(id+"F3.wireOp",EDGE,"4a1b5445-5559-461f-b6f1-b4cd9b95ea10")])]});
            var Q4;
            Q4=makeQuery(id+"F1.opRevolve","SWEPT_BODY",BODY,{"disambiguationData":[OSD([sQuery(id+"F0.wireOp",EDGE,"E0"),sQuery(id+"F0.wireOp",EDGE,"E1")])]});
            var Q5;
            Q5=qCreatedBy(makeId("Origin.pointOp"),VERTEX);
            transform(context, id + "F5", {"entities" : qUnion([Q0, Q1, Q2, Q3, Q4]), "transformType" : TransformType.SCALE_UNIFORMLY, "scale" : 0.03, "scalePoint" : qUnion([Q5]), "makeCopy" : false});
        }
        {
            var Q0;
            Q0=qCreatedBy(makeId("Top.planeOp"),FACE);
            var sketch = newSketch(context, id + "F6", { "sketchPlane" : qUnion([Q0])});
            skLineSegment(sketch, "E150", {"start": v(0, 15) * mm, "end": v(0, -15) * mm});
            skArc(sketch, "E151", {"start": v(0, 15) * mm, "mid": v(-15, 0) * mm, "end": v(0, -15) * mm});
            skArc(sketch, "E152", {"start": v(0, 10.25) * mm, "mid": v(-10.25, 0) * mm, "end": v(0, -10.25) * mm});
            skArc(sketch, "E153", {"start": v(0, 7) * mm, "mid": v(-7, 0) * mm, "end": v(0, -7) * mm});
            skSolve(sketch);
        }
        {
            var Q0;
            {var subQ0=sQuery(id+"F6.wireOp",EDGE,"E151");Q0=makeQuery(id+"F6.imprint","IMPRINT",FACE,{"disambiguationData":[TD([[makeQuery(id+"F6.imprint","IMPRINT",EDGE,{"derivedFrom":subQ0}),1.0]])]});}
            var Q1;
            {var subQ0=sQuery(id+"F6.wireOp",EDGE,"E153");Q1=makeQuery(id+"F6.imprint","IMPRINT",FACE,{"disambiguationData":[TD([[makeQuery(id+"F6.imprint","IMPRINT",EDGE,{"derivedFrom":subQ0}),1.0]])]});}
            var Q2;
            Q2=sQuery(id+"F6.wireOp",EDGE,"E150");
            revolve(context, id + "F7", {"operationType" : NewBodyOperationType.REMOVE, "entities" : qUnion([Q0, Q1]), "axis" : qUnion([Q2]), "revolveType" : RevolveType.FULL});
        }
        {
            var Q0;
            Q0=makeQuery(id+"F1.opRevolve","SWEPT_BODY",BODY,{"disambiguationData":[OSD([sQuery(id+"F0.wireOp",EDGE,"E0"),sQuery(id+"F0.wireOp",EDGE,"E1")])]});
            var Q1;
            Q1=sQuery(id+"F0.wireOp",VERTEX,"E1.center");
            transform(context, id + "F8", {"entities" : qUnion([Q0]), "transformType" : TransformType.SCALE_UNIFORMLY, "scale" : 1.4, "scalePoint" : qUnion([Q1]), "makeCopy" : false});
        }
        {
            var Q0;
            Q0=qCreatedBy(makeId("Front.planeOp"),FACE);
            var sketch = newSketch(context, id + "F9", { "sketchPlane" : qUnion([Q0])});
            skCircle(sketch, "E154", {"center": v(0, -5.12) * mm, "radius": 2 * mm});
            skSolve(sketch);
        }
        {
            var Q0;
            Q0=qSketchRegion(id+"F9",true);
            extrude(context, id + "F10", {"entities" : qUnion([Q0]), "operationType" : NewBodyOperationType.REMOVE, "oppositeDirection" : true, "depth" : 25 * mm});
        }
    });
